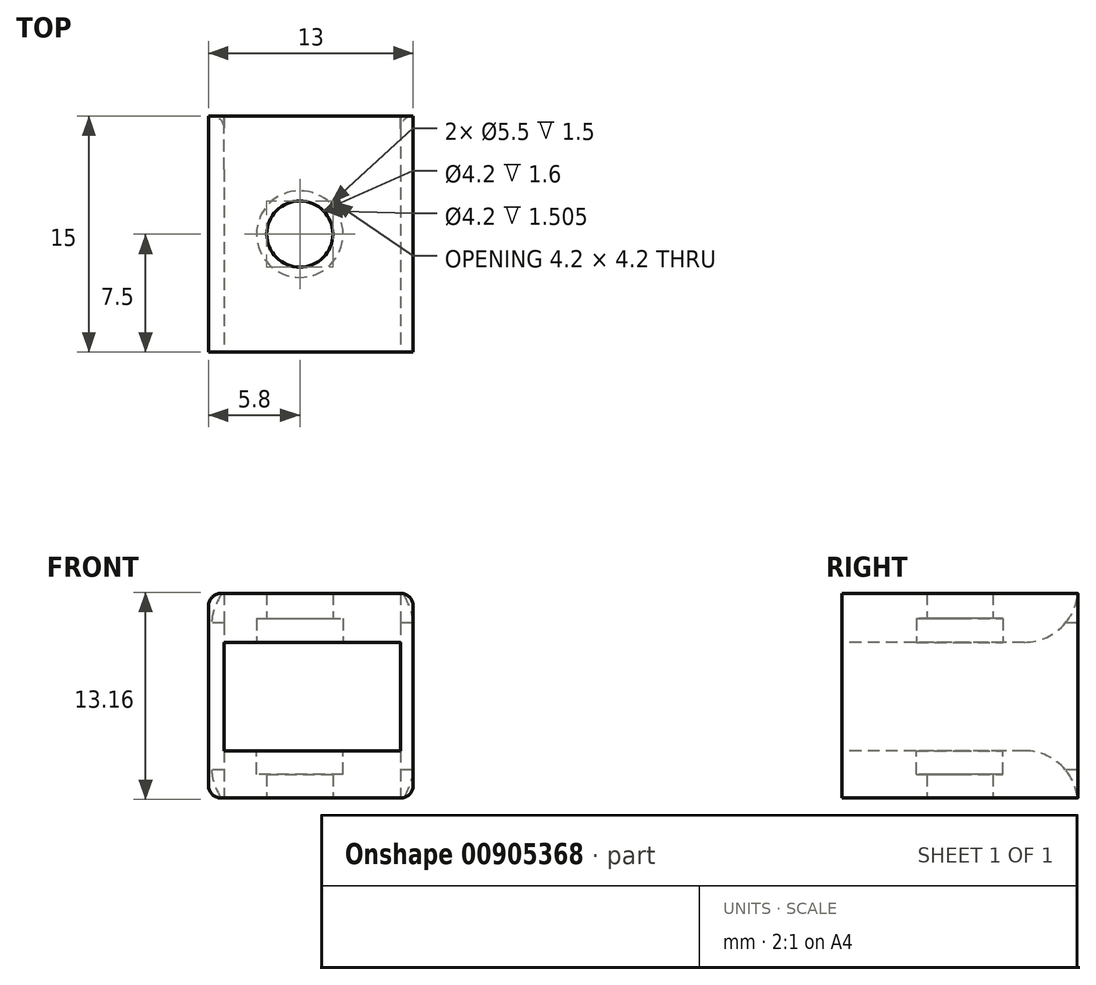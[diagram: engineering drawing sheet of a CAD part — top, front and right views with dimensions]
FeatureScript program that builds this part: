
annotation { "Feature Type Name" : "Feature", "Feature Type Description" : "" }
export const myFeature = defineFeature(function(context is Context, id is Id, definition is map)
    precondition{}
    {
        {
            var Q0;
            Q0=qCreatedBy(makeId("Top.planeOp"),FACE);
            var sketch = newSketch(context, id + "F0", { "sketchPlane" : qUnion([Q0])});
            skLineSegment(sketch, "E0.bottom", {"start": v(0, 0) * mm, "end": v(-13, 0) * mm});
            skLineSegment(sketch, "E0.top", {"start": v(0, 15) * mm, "end": v(-13, 15) * mm});
            skLineSegment(sketch, "E0.left", {"start": v(0, 0) * mm, "end": v(0, 15) * mm});
            skLineSegment(sketch, "E0.right", {"start": v(-13, 0) * mm, "end": v(-13, 15) * mm});
            skCircle(sketch, "E1", {"center": v(-7.2, 7.5) * mm, "radius": 2.1 * mm});
            skPoint(sketch, "E1.centerSnap0", {"position": v(-6.5, 15) * mm});
            skPoint(sketch, "E1.centerSnap1", {"position": v(-13, 7.5) * mm});
            skCircle(sketch, "E2", {"center": v(-7.2, 7.5) * mm, "radius": 2.75 * mm});
            skLineSegment(sketch, "E3", {"start": v(-13, 7.5) * mm, "end": v(-7.2, 7.5) * mm});
            skSolve(sketch);
        }
        {
            var Q0;
            Q0 = qSketchRegion(id + "F0", true);
            var Q1;
            Q1=makeQuery(id+"F0.imprint","IMPRINT",FACE,{"disambiguationData":[TD([[makeQuery(id+"F0.imprint","IMPRINT",EDGE,{"derivedFrom":sQuery(id+"F0.wireOp",EDGE,"E1")}),-1.0]])]});
            extrude(context, id + "F1", {"entities" : qUnion([Q0, Q1]), "depth" : 13 * mm, "offsetDistance" : 25 * mm});
        }
        {
            var Q0;
            Q0=makeQuery(id+"F1.opExtrude","SWEPT_FACE",FACE,{"disambiguationData":[OSD([sQuery(id+"F0.wireOp",EDGE,"E0.bottom")])]});
            var sketch = newSketch(context, id + "F2", { "sketchPlane" : qUnion([Q0])});
            skLineSegment(sketch, "E4", {"start": v(-12.07, 13) * mm, "end": v(-12.07, 11.4) * mm, "construction": true});
            skLineSegment(sketch, "E5", {"start": v(-13, 6.83) * mm, "end": v(-12, 6.83) * mm, "construction": true});
            skLineSegment(sketch, "E6", {"start": v(0, 6.86) * mm, "end": v(-1, 6.86) * mm, "construction": true});
            skLineSegment(sketch, "E7", {"start": v(-6.5, 0) * mm, "end": v(-6.5, 1.6) * mm, "construction": true});
            skLineSegment(sketch, "E8", {"start": v(-13, 12.25) * mm, "end": v(-12, 12.25) * mm, "construction": true});
            skLineSegment(sketch, "E9.bottom", {"start": v(-12, 11.4) * mm, "end": v(-0.8, 11.4) * mm});
            skLineSegment(sketch, "E9.top", {"start": v(-12, 1.5) * mm, "end": v(-0.8, 1.5) * mm});
            skLineSegment(sketch, "E9.left", {"start": v(-12, 11.4) * mm, "end": v(-12, 1.5) * mm});
            skLineSegment(sketch, "E9.right", {"start": v(-0.8, 11.4) * mm, "end": v(-0.8, 1.5) * mm});
            skLineSegment(sketch, "E10", {"start": v(-11.08, 1.5) * mm, "end": v(-11.08, 3) * mm, "construction": true});
            skLineSegment(sketch, "E11", {"start": v(-10.88, 11.4) * mm, "end": v(-10.88, 9.9) * mm, "construction": true});
            skLineSegment(sketch, "E12", {"start": v(-12, 3) * mm, "end": v(-0.8, 3) * mm});
            skLineSegment(sketch, "E13", {"start": v(-12, 9.9) * mm, "end": v(-0.8, 9.9) * mm});
            skSolve(sketch);
        }
        {
            var Q0;
            {var subQ0=sQuery(id+"F2.wireOp",EDGE,"E12");Q0=makeQuery(id+"F2.imprint","IMPRINT",FACE,{"disambiguationData":[TD([[makeQuery(id+"F2.imprint","IMPRINT",EDGE,{"derivedFrom":subQ0}),1.0]])]});}
            extrude(context, id + "F3", {"entities" : qUnion([Q0]), "operationType" : NewBodyOperationType.REMOVE, "oppositeDirection" : true, "depth" : 25 * mm, "offsetDistance" : 25 * mm});
        }
        {
            var Q0;
            Q0=makeQuery(id+"F1.opExtrude","CAP_EDGE",EDGE,{"disambiguationData":[OSD([sQuery(id+"F0.wireOp",EDGE,"E0.right")])],"isStart":true});
            var Q1;
            Q1=makeQuery(id+"F1.opExtrude","CAP_EDGE",EDGE,{"disambiguationData":[OSD([sQuery(id+"F0.wireOp",EDGE,"E0.left")])],"isStart":true});
            var Q2;
            Q2=makeQuery(id+"F1.opExtrude","CAP_EDGE",EDGE,{"disambiguationData":[OSD([sQuery(id+"F0.wireOp",EDGE,"E0.right")])],"isStart":false});
            var Q3;
            Q3=makeQuery(id+"F1.opExtrude","CAP_EDGE",EDGE,{"disambiguationData":[OSD([sQuery(id+"F0.wireOp",EDGE,"E0.left")])],"isStart":false});
            fillet(context, id + "F4", {"entities" : qUnion([Q0, Q1, Q2, Q3]), "radius" : 0.8 * mm, "tangentPropagation" : true, "allowEdgeOverflow" : false});
        }
        {
            var Q0;
            Q0=makeQuery(id+"F3.boolean.opBoolean","COPY",FACE,{"derivedFrom":makeQuery(id+"F3.opExtrude","SWEPT_FACE",FACE,{"disambiguationData":[OSD([sQuery(id+"F2.wireOp",EDGE,"E12")])]})});
            var sketch = newSketch(context, id + "F5", { "sketchPlane" : qUnion([Q0])});
            skCircle(sketch, "E14", {"center": v(-7.2, 7.5) * mm, "radius": 2.75 * mm});
            skSolve(sketch);
        }
        {
            var Q0;
            Q0=makeQuery(id+"F5.imprint","IMPRINT",FACE,{"disambiguationData":[TD([[makeQuery(id+"F5.imprint","IMPRINT",EDGE,{"derivedFrom":sQuery(id+"F5.wireOp",EDGE,"E14")}),1.0]])]});
            var Q1;
            Q1=sQuery(id+"F5.wireOp",EDGE,"E14");
            extrude(context, id + "F6", {"entities" : qUnion([Q0]), "operationType" : NewBodyOperationType.REMOVE, "surfaceEntities" : qUnion([Q1]), "oppositeDirection" : true, "depth" : 1.5 * mm, "offsetDistance" : 25 * mm});
        }
        {
            var Q0;
            Q0=makeQuery(id+"F3.boolean.opBoolean","COPY",FACE,{"derivedFrom":makeQuery(id+"F3.opExtrude","SWEPT_FACE",FACE,{"disambiguationData":[OSD([sQuery(id+"F2.wireOp",EDGE,"E13")])]})});
            var sketch = newSketch(context, id + "F7", { "sketchPlane" : qUnion([Q0])});
            skCircle(sketch, "E15", {"center": v(-7.2, -7.5) * mm, "radius": 2.75 * mm});
            skSolve(sketch);
        }
        {
            var Q0;
            Q0=makeQuery(id+"F7.imprint","IMPRINT",FACE,{"disambiguationData":[TD([[makeQuery(id+"F7.imprint","IMPRINT",EDGE,{"derivedFrom":sQuery(id+"F7.wireOp",EDGE,"E15")}),1.0]])]});
            extrude(context, id + "F8", {"entities" : qUnion([Q0]), "operationType" : NewBodyOperationType.REMOVE, "oppositeDirection" : true, "depth" : 1.5 * mm, "offsetDistance" : 25 * mm});
        }
        {
            var Q0;
            Q0=makeQuery(id+"F3.boolean.opBoolean","COPY",EDGE,{"derivedFrom":makeQuery(id+"F3.opExtrude","CAP_EDGE",EDGE,{"disambiguationData":[OSD([sQuery(id+"F2.wireOp",EDGE,"E12")])],"isStart":true})});
            var Q1;
            Q1=makeQuery(id+"F3.boolean.opBoolean","COPY",EDGE,{"derivedFrom":makeQuery(id+"F3.opExtrude","CAP_EDGE",EDGE,{"disambiguationData":[OSD([sQuery(id+"F2.wireOp",EDGE,"E13")])],"isStart":true})});
            var Q2;
            Q2=makeQuery(id+"F3.boolean.opBoolean","INTERSECT",EDGE,{"derivedFrom":[makeQuery(id+"F1.opExtrude","SWEPT_FACE",FACE,{"disambiguationData":[OSD([sQuery(id+"F0.wireOp",EDGE,"E0.top")])]}),makeQuery(id+"F3.opExtrude","SWEPT_FACE",FACE,{"disambiguationData":[OSD([sQuery(id+"F2.wireOp",EDGE,"E13")])]})]});
            var Q3;
            Q3=makeQuery(id+"F3.boolean.opBoolean","INTERSECT",EDGE,{"derivedFrom":[makeQuery(id+"F1.opExtrude","SWEPT_FACE",FACE,{"disambiguationData":[OSD([sQuery(id+"F0.wireOp",EDGE,"E0.top")])]}),makeQuery(id+"F3.opExtrude","SWEPT_FACE",FACE,{"disambiguationData":[OSD([sQuery(id+"F2.wireOp",EDGE,"E12")])]})]});
            fillet(context, id + "F9", {"entities" : qUnion([Q0, Q1, Q2, Q3]), "radius" : 3.4 * mm, "tangentPropagation" : true, "allowEdgeOverflow" : false});
        }
        {
            var Q0;
            Q0=makeQuery(id+"F3.boolean.opBoolean","INTERSECT",EDGE,{"derivedFrom":[makeQuery(id+"F1.opExtrude","SWEPT_FACE",FACE,{"disambiguationData":[OSD([sQuery(id+"F0.wireOp",EDGE,"E0.top")])]}),makeQuery(id+"F3.opExtrude","SWEPT_FACE",FACE,{"disambiguationData":[OSD([sQuery(id+"F2.wireOp",EDGE,"E9.left")])]})]});
            var Q1;
            Q1=makeQuery(id+"F3.boolean.opBoolean","COPY",EDGE,{"derivedFrom":makeQuery(id+"F3.opExtrude","CAP_EDGE",EDGE,{"disambiguationData":[OSD([sQuery(id+"F2.wireOp",EDGE,"E9.right")])],"isStart":true})});
            var Q2;
            Q2=makeQuery(id+"F3.boolean.opBoolean","COPY",EDGE,{"derivedFrom":makeQuery(id+"F3.opExtrude","CAP_EDGE",EDGE,{"disambiguationData":[OSD([sQuery(id+"F2.wireOp",EDGE,"E9.left")])],"isStart":true})});
            var Q3;
            Q3=makeQuery(id+"F3.boolean.opBoolean","INTERSECT",EDGE,{"derivedFrom":[makeQuery(id+"F1.opExtrude","SWEPT_FACE",FACE,{"disambiguationData":[OSD([sQuery(id+"F0.wireOp",EDGE,"E0.top")])]}),makeQuery(id+"F3.opExtrude","SWEPT_FACE",FACE,{"disambiguationData":[OSD([sQuery(id+"F2.wireOp",EDGE,"E9.right")])]})]});
            fillet(context, id + "F10", {"entities" : qUnion([Q0, Q1, Q2, Q3]), "radius" : 0.8 * mm, "tangentPropagation" : true, "allowEdgeOverflow" : false});
        }
    });
